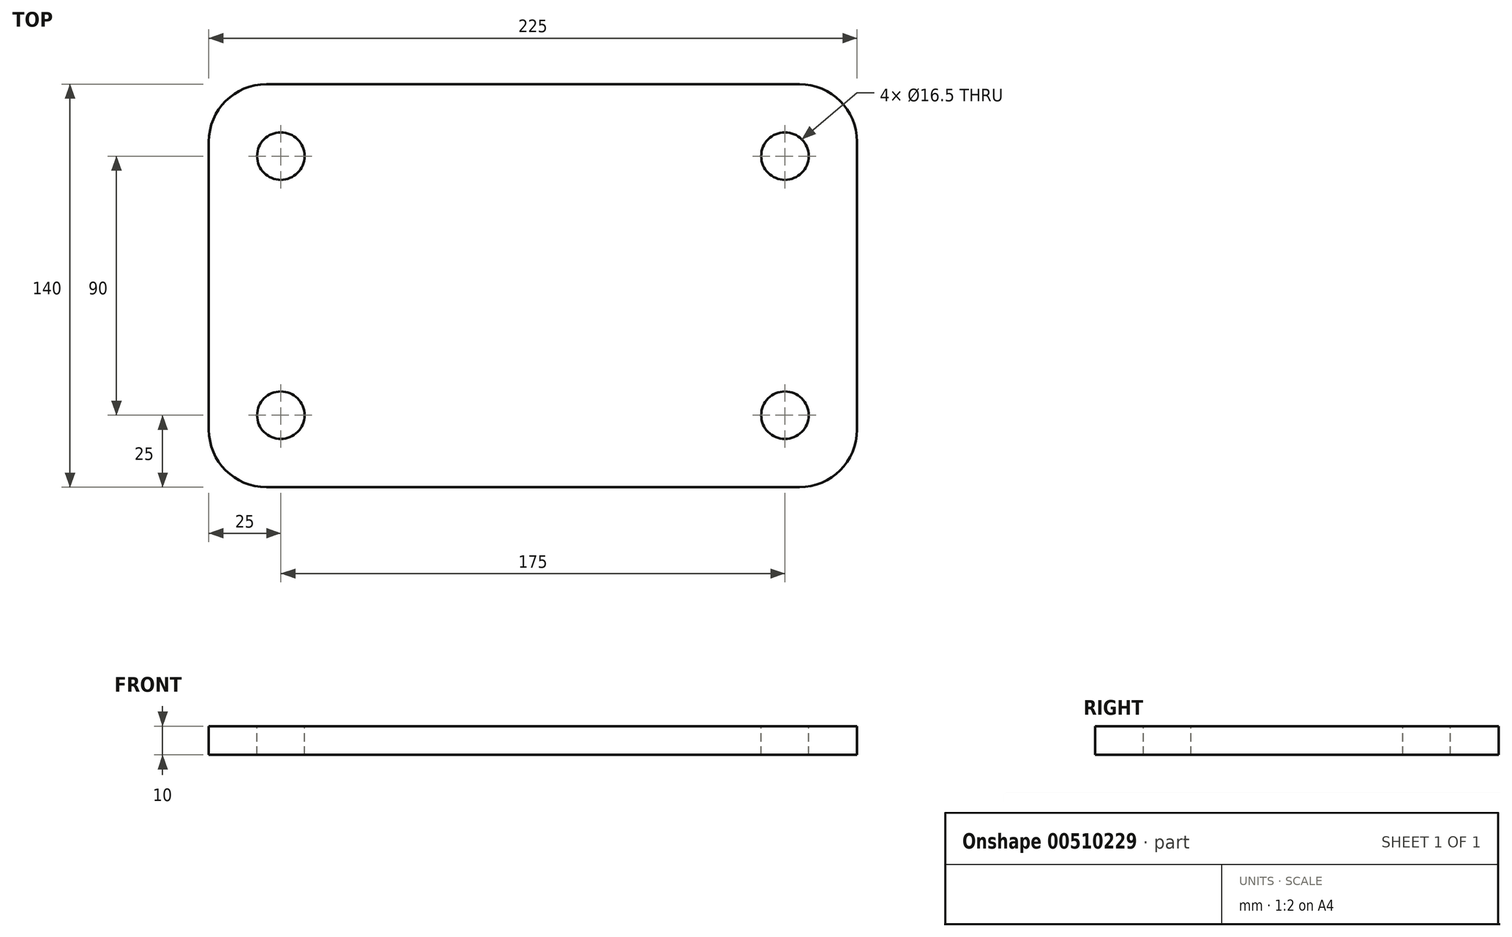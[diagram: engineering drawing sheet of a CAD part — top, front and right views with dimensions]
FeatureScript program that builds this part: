
annotation { "Feature Type Name" : "Feature", "Feature Type Description" : "" }
export const myFeature = defineFeature(function(context is Context, id is Id, definition is map)
    precondition{}
    {
        {
            var Q0;
            Q0=qCreatedBy(makeId("Top.planeOp"),FACE);
            var sketch = newSketch(context, id + "F0", { "sketchPlane" : qUnion([Q0])});
            skLineSegment(sketch, "E0.bottom", {"start": v(92.5, 70) * mm, "end": v(-92.5, 70) * mm});
            skLineSegment(sketch, "E0.top", {"start": v(92.5, -70) * mm, "end": v(-92.5, -70) * mm});
            skLineSegment(sketch, "E0.left", {"start": v(112.5, 50) * mm, "end": v(112.5, -50) * mm});
            skLineSegment(sketch, "E0.right", {"start": v(-112.5, 50) * mm, "end": v(-112.5, -50) * mm});
            skPoint(sketch, "E0.middle", {"position": v(0, 0) * mm});
            skPoint(sketch, "E1.visualSharp", {"position": v(-112.5, 70) * mm});
            skArc(sketch, "E1.filletArc", {"start": v(-92.5, 70) * mm, "mid": v(-106.64, 64.14) * mm, "end": v(-112.5, 50) * mm});
            skPoint(sketch, "E2.visualSharp", {"position": v(112.5, 70) * mm});
            skArc(sketch, "E2.filletArc", {"start": v(112.5, 50) * mm, "mid": v(106.64, 64.14) * mm, "end": v(92.5, 70) * mm});
            skPoint(sketch, "E3.visualSharp", {"position": v(112.5, -70) * mm});
            skArc(sketch, "E3.filletArc", {"start": v(92.5, -70) * mm, "mid": v(106.64, -64.14) * mm, "end": v(112.5, -50) * mm});
            skPoint(sketch, "E4.visualSharp", {"position": v(-112.5, -70) * mm});
            skArc(sketch, "E4.filletArc", {"start": v(-112.5, -50) * mm, "mid": v(-106.64, -64.14) * mm, "end": v(-92.5, -70) * mm});
            skSolve(sketch);
        }
        {
            var Q0;
            Q0 = qSketchRegion(id + "F0", true);
            extrude(context, id + "F1", {"entities" : qUnion([Q0]), "depth" : 10 * mm});
        }
        {
            var Q0;
            Q0=makeQuery(id+"F1.opExtrude","CAP_FACE",FACE,{"disambiguationData":[OSD([sQuery(id+"F0.wireOp",EDGE,"E0.bottom"),sQuery(id+"F0.wireOp",EDGE,"E0.top"),sQuery(id+"F0.wireOp",EDGE,"E0.left"),sQuery(id+"F0.wireOp",EDGE,"E0.right"),sQuery(id+"F0.wireOp",EDGE,"E1.filletArc"),sQuery(id+"F0.wireOp",EDGE,"E2.filletArc"),sQuery(id+"F0.wireOp",EDGE,"E3.filletArc"),sQuery(id+"F0.wireOp",EDGE,"E4.filletArc")])],"isStart":false});
            var sketch = newSketch(context, id + "F2", { "sketchPlane" : qUnion([Q0])});
            skCircle(sketch, "E5", {"center": v(-87.5, 45) * mm, "radius": 8.25 * mm});
            skLineSegment(sketch, "E6", {"start": v(0, 0) * mm, "end": v(0, 30.46) * mm, "construction": true});
            skLineSegment(sketch, "E7", {"start": v(0, 0) * mm, "end": v(-27.68, 0) * mm, "construction": true});
            skCircle(sketch, "E8.MirrorC", {"center": v(87.5, 45) * mm, "radius": 8.25 * mm});
            skCircle(sketch, "E9.MirrorC", {"center": v(-87.5, -45) * mm, "radius": 8.25 * mm});
            skCircle(sketch, "E10.MirrorC", {"center": v(87.5, -45) * mm, "radius": 8.25 * mm});
            skSolve(sketch);
        }
        {
            var Q0;
            Q0 = qSketchRegion(id + "F2", true);
            extrude(context, id + "F3", {"entities" : qUnion([Q0]), "operationType" : NewBodyOperationType.REMOVE, "endBound" : BoundingType.THROUGH_ALL, "oppositeDirection" : true, "depth" : 25 * mm});
        }
    });
